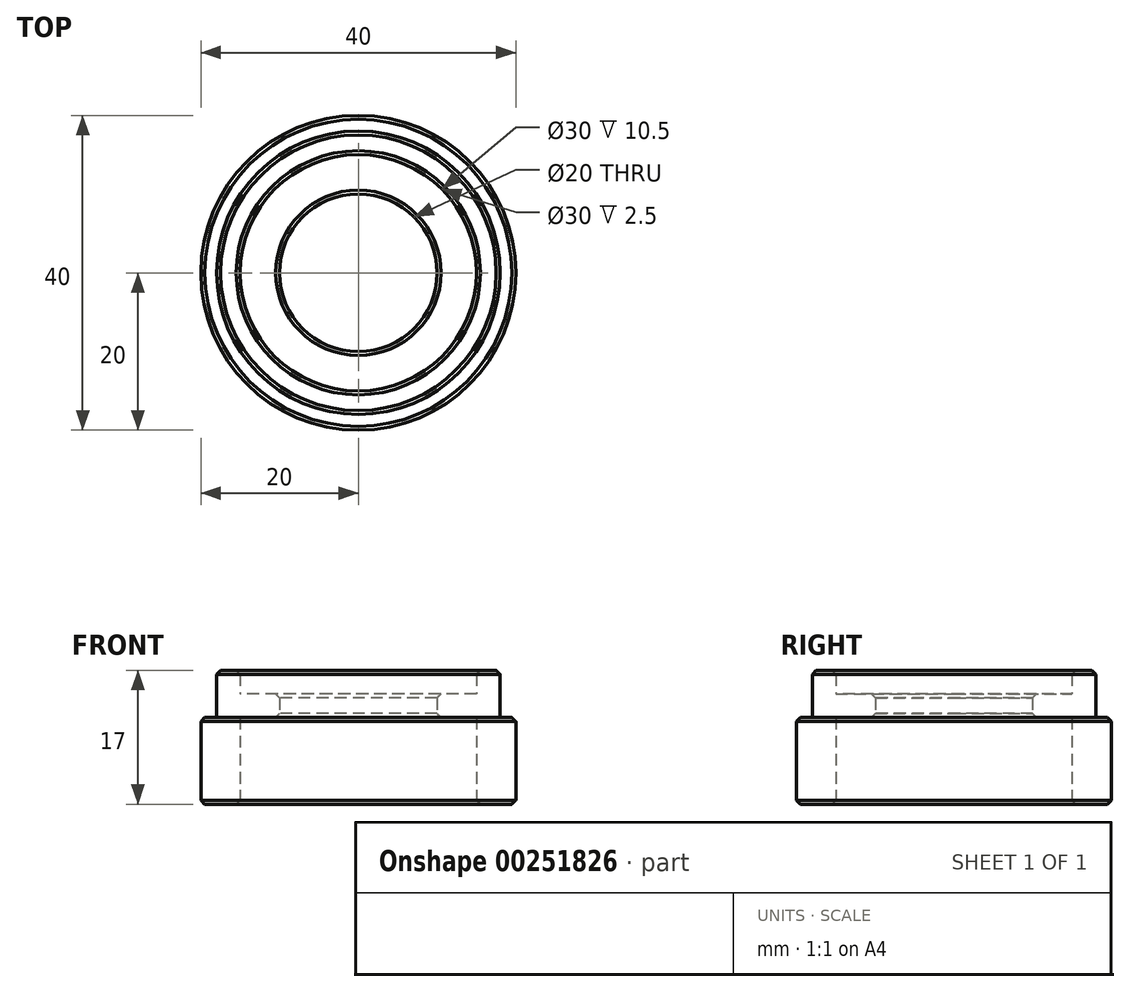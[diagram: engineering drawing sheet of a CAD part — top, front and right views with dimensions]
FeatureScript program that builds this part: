
annotation { "Feature Type Name" : "Feature", "Feature Type Description" : "" }
export const myFeature = defineFeature(function(context is Context, id is Id, definition is map)
    precondition{}
    {
        {
            var Q0;
            Q0=qCreatedBy(makeId("Top.planeOp"),FACE);
            var sketch = newSketch(context, id + "F0", { "sketchPlane" : qUnion([Q0])});
            skCircle(sketch, "E0", {"center": v(0, 0) * mm, "radius": 20 * mm});
            skCircle(sketch, "E1", {"center": v(0, 0) * mm, "radius": 15 * mm});
            skSolve(sketch);
        }
        {
            var Q0;
            Q0=makeQuery(id+"F0.imprint","IMPRINT",FACE,{"disambiguationData":[TD([[makeQuery(id+"F0.imprint","IMPRINT",EDGE,{"derivedFrom":sQuery(id+"F0.wireOp",EDGE,"E0")}),1.0]])]});
            extrude(context, id + "F1", {"entities" : qUnion([Q0]), "depth" : 11 * mm});
        }
        {
            var Q0;
            Q0=makeQuery(id+"F1.opExtrude","CAP_FACE",FACE,{"disambiguationData":[OSD([sQuery(id+"F0.wireOp",EDGE,"E0"),sQuery(id+"F0.wireOp",EDGE,"E1")])],"isStart":false});
            var sketch = newSketch(context, id + "F2", { "sketchPlane" : qUnion([Q0])});
            skCircle(sketch, "E2", {"center": v(0, 0) * mm, "radius": 18 * mm});
            skCircle(sketch, "E3", {"center": v(0, 0) * mm, "radius": 10 * mm});
            skSolve(sketch);
        }
        {
            var Q0;
            Q0=makeQuery(id+"F2.imprint","IMPRINT",FACE,{"disambiguationData":[TD([[makeQuery(id+"F2.imprint","IMPRINT",EDGE,{"derivedFrom":sQuery(id+"F2.wireOp",EDGE,"E2")}),1.0]])]});
            var Q1;
            Q1=makeQuery(id+"F2.imprint","IMPRINT",FACE,{"disambiguationData":[TD([[makeQuery(id+"F2.imprint","IMPRINT",EDGE,{"derivedFrom":sQuery(id+"F2.wireOp",EDGE,"E3")}),-1.0]])]});
            extrude(context, id + "F3", {"entities" : qUnion([Q0, Q1]), "operationType" : NewBodyOperationType.ADD, "depth" : 3 * mm});
        }
        {
            var Q0;
            Q0=makeQuery(id+"F3.opExtrude","CAP_FACE",FACE,{"disambiguationData":[OSD([sQuery(id+"F2.wireOp",EDGE,"E2"),sQuery(id+"F2.wireOp",EDGE,"E3")])],"isStart":false});
            var sketch = newSketch(context, id + "F4", { "sketchPlane" : qUnion([Q0])});
            skCircle(sketch, "E4", {"center": v(0, 0) * mm, "radius": 18 * mm});
            skCircle(sketch, "E5", {"center": v(0, 0) * mm, "radius": 15 * mm});
            skSolve(sketch);
        }
        {
            var Q0;
            Q0 = qSketchRegion(id + "F4", true);
            extrude(context, id + "F5", {"entities" : qUnion([Q0]), "operationType" : NewBodyOperationType.ADD, "depth" : 3 * mm});
        }
        {
            var Q0;
            Q0=makeQuery(id+"F1.opExtrude","CAP_EDGE",EDGE,{"disambiguationData":[OSD([sQuery(id+"F0.wireOp",EDGE,"E0")])],"isStart":true});
            var Q1;
            Q1=makeQuery(id+"F1.opExtrude","CAP_EDGE",EDGE,{"disambiguationData":[OSD([sQuery(id+"F0.wireOp",EDGE,"E1")])],"isStart":true});
            var Q2;
            Q2=makeQuery(id+"F1.opExtrude","CAP_EDGE",EDGE,{"disambiguationData":[OSD([sQuery(id+"F0.wireOp",EDGE,"E0")])],"isStart":false});
            var Q3;
            Q3=makeQuery(id+"F5.opExtrude","CAP_EDGE",EDGE,{"disambiguationData":[OSD([sQuery(id+"F4.wireOp",EDGE,"E4")])],"isStart":false});
            var Q4;
            Q4=makeQuery(id+"F5.opExtrude","CAP_EDGE",EDGE,{"disambiguationData":[OSD([sQuery(id+"F4.wireOp",EDGE,"E5")])],"isStart":false});
            var Q5;
            Q5=makeQuery(id+"F3.opExtrude","CAP_EDGE",EDGE,{"disambiguationData":[OSD([sQuery(id+"F2.wireOp",EDGE,"E3")])],"isStart":false});
            chamfer(context, id + "F6", {"entities" : qUnion([Q0, Q1, Q2, Q3, Q4, Q5]), "width" : .5 * mm, "tangentPropagation" : true});
        }
        {
            var Q0;
            Q0=makeQuery(id+"F3.opExtrude","CAP_EDGE",EDGE,{"disambiguationData":[OSD([sQuery(id+"F2.wireOp",EDGE,"E3")])],"isStart":true});
            chamfer(context, id + "F7", {"entities" : qUnion([Q0]), "width" : .5 * mm, "tangentPropagation" : true});
        }
    });
